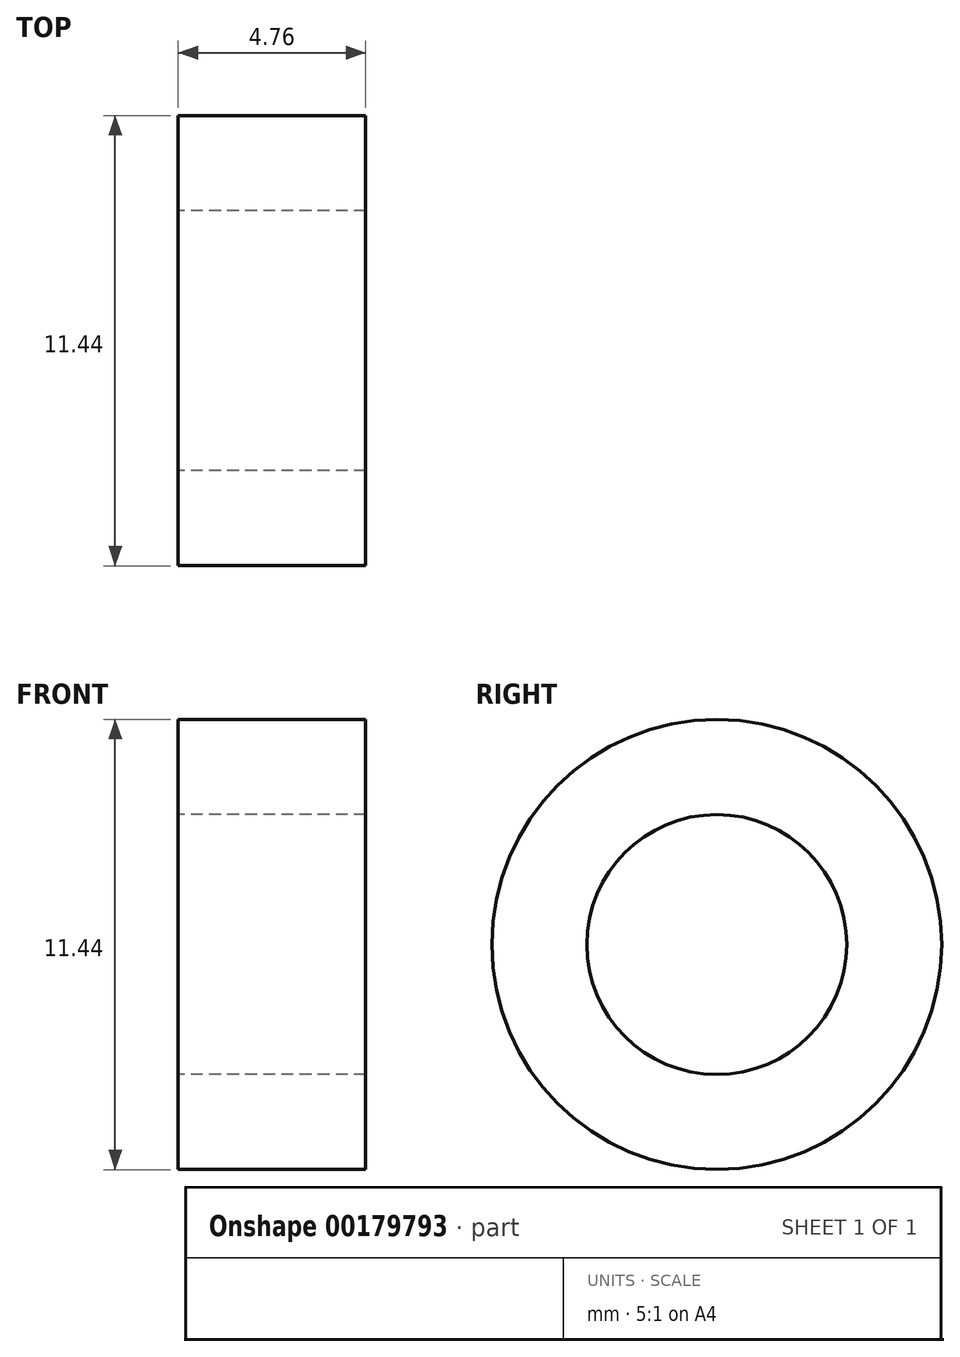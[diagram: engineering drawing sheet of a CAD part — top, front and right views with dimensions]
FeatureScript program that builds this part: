
annotation { "Feature Type Name" : "Feature", "Feature Type Description" : "" }
export const myFeature = defineFeature(function(context is Context, id is Id, definition is map)
    precondition{}
    {
        {
            var Q0;
            Q0=qCreatedBy(makeId("Right.planeOp"),FACE);
            var sketch = newSketch(context, id + "F0", { "sketchPlane" : qUnion([Q0])});
            skCircle(sketch, "E0", {"center": v(0, 0) * mm, "radius": 3.3 * mm});
            skCircle(sketch, "E1", {"center": v(0, 0) * mm, "radius": 5.72 * mm});
            skSolve(sketch);
        }
        {
            var Q0;
            Q0=makeQuery(id+"F0.imprint","IMPRINT",FACE,{"disambiguationData":[TD([[makeQuery(id+"F0.imprint","IMPRINT",EDGE,{"derivedFrom":sQuery(id+"F0.wireOp",EDGE,"E0")}),-1.0]])]});
            extrude(context, id + "F1", {"entities" : qUnion([Q0]), "endBound" : BoundingType.SYMMETRIC, "depth" : 4.76 * mm});
        }
    });
